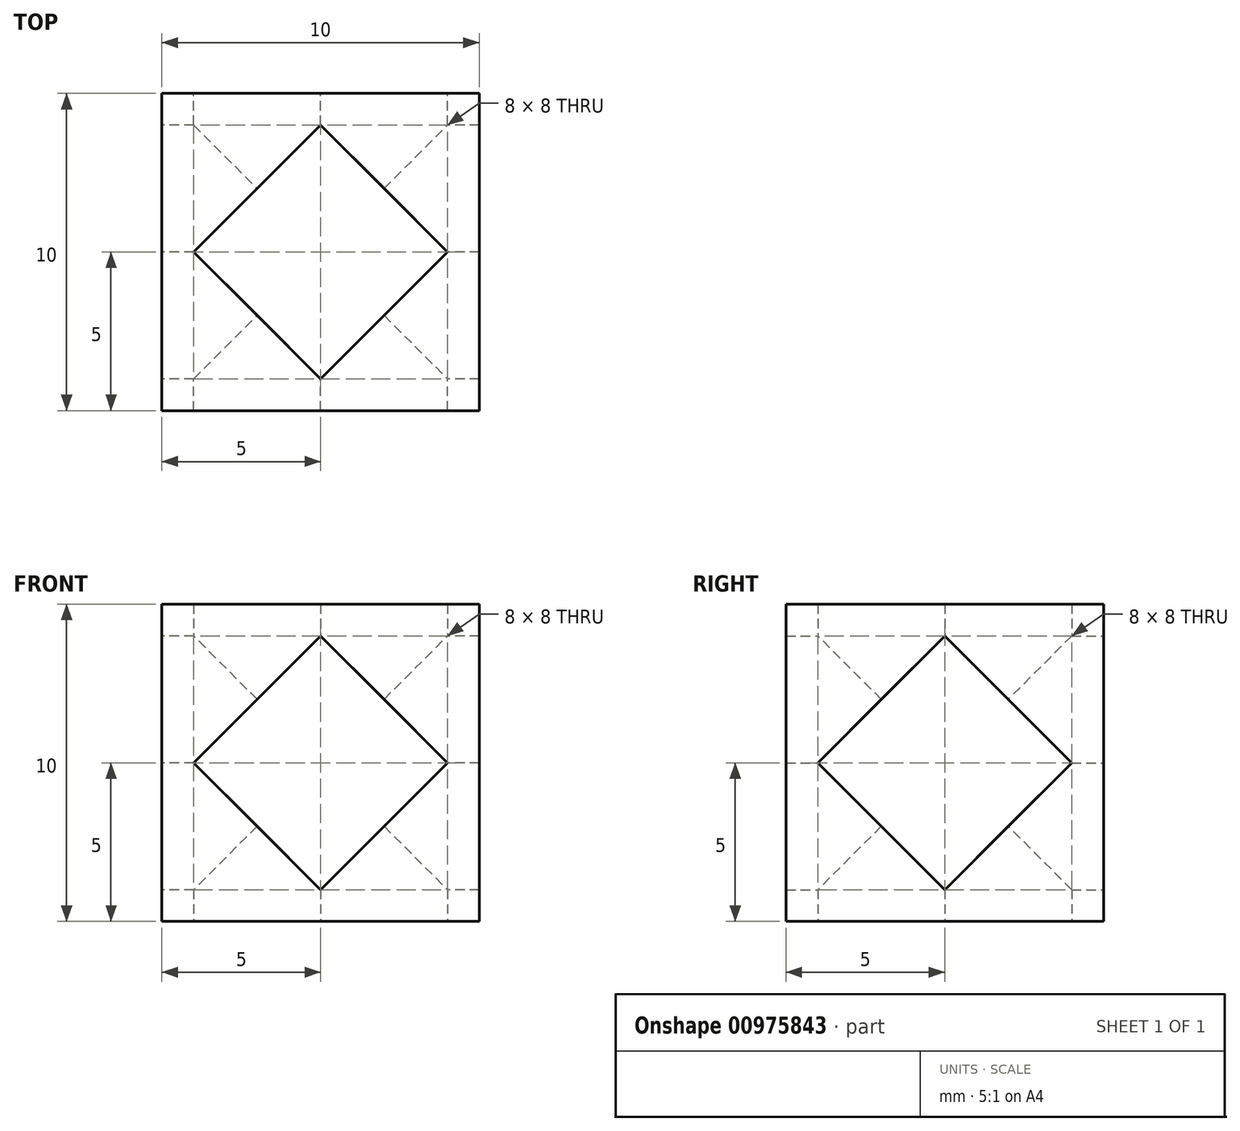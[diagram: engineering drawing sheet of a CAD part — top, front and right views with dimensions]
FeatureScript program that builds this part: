
annotation { "Feature Type Name" : "Feature", "Feature Type Description" : "" }
export const myFeature = defineFeature(function(context is Context, id is Id, definition is map)
    precondition{}
    {
        {
            var Q0;
            Q0=qCreatedBy(makeId("Front.planeOp"),FACE);
            var sketch = newSketch(context, id + "F0", { "sketchPlane" : qUnion([Q0])});
            skLineSegment(sketch, "E0.bottom", {"start": v(5, 5) * mm, "end": v(-5, 5) * mm});
            skLineSegment(sketch, "E0.top", {"start": v(5, -5) * mm, "end": v(-5, -5) * mm});
            skLineSegment(sketch, "E0.left", {"start": v(5, 5) * mm, "end": v(5, -5) * mm});
            skLineSegment(sketch, "E0.right", {"start": v(-5, 5) * mm, "end": v(-5, -5) * mm});
            skPoint(sketch, "E0.middle", {"position": v(0, 0) * mm});
            skLineSegment(sketch, "E1", {"start": v(0, 4) * mm, "end": v(-4, 0) * mm});
            skLineSegment(sketch, "E2", {"start": v(-4, 0) * mm, "end": v(0, -4) * mm});
            skLineSegment(sketch, "E3", {"start": v(0, -4) * mm, "end": v(4, 0) * mm});
            skLineSegment(sketch, "E4", {"start": v(4, 0) * mm, "end": v(0, 4) * mm});
            skSolve(sketch);
        }
        {
            var Q0;
            Q0=qCreatedBy(makeId("Right.planeOp"),FACE);
            var sketch = newSketch(context, id + "F1", { "sketchPlane" : qUnion([Q0])});
            skLineSegment(sketch, "E5.bottom", {"start": v(5, 5) * mm, "end": v(-5, 5) * mm});
            skLineSegment(sketch, "E5.top", {"start": v(5, -5) * mm, "end": v(-5, -5) * mm});
            skLineSegment(sketch, "E5.left", {"start": v(5, 5) * mm, "end": v(5, -5) * mm});
            skLineSegment(sketch, "E5.right", {"start": v(-5, 5) * mm, "end": v(-5, -5) * mm});
            skPoint(sketch, "E5.middle", {"position": v(0, 0) * mm});
            skLineSegment(sketch, "E6", {"start": v(0, 4) * mm, "end": v(-4, 0) * mm});
            skLineSegment(sketch, "E7", {"start": v(-4, 0) * mm, "end": v(0, -4) * mm});
            skLineSegment(sketch, "E8", {"start": v(0, -4) * mm, "end": v(4, 0) * mm});
            skLineSegment(sketch, "E9", {"start": v(4, 0) * mm, "end": v(0, 4) * mm});
            skSolve(sketch);
        }
        {
            var Q0;
            Q0=qCreatedBy(makeId("Top.planeOp"),FACE);
            var sketch = newSketch(context, id + "F2", { "sketchPlane" : qUnion([Q0])});
            skLineSegment(sketch, "E10.bottom", {"start": v(5, 5) * mm, "end": v(-5, 5) * mm});
            skLineSegment(sketch, "E10.top", {"start": v(5, -5) * mm, "end": v(-5, -5) * mm});
            skLineSegment(sketch, "E10.left", {"start": v(5, 5) * mm, "end": v(5, -5) * mm});
            skLineSegment(sketch, "E10.right", {"start": v(-5, 5) * mm, "end": v(-5, -5) * mm});
            skPoint(sketch, "E10.middle", {"position": v(0, 0) * mm});
            skLineSegment(sketch, "E11", {"start": v(0, 4) * mm, "end": v(-4, 0) * mm});
            skLineSegment(sketch, "E12", {"start": v(-4, 0) * mm, "end": v(0, -4) * mm});
            skLineSegment(sketch, "E13", {"start": v(0, -4) * mm, "end": v(4, 0) * mm});
            skLineSegment(sketch, "E14", {"start": v(4, 0) * mm, "end": v(0, 4) * mm});
            skSolve(sketch);
        }
        {
            var Q0;
            Q0 = qSketchRegion(id + "F0", true);
            extrude(context, id + "F3", {"entities" : qUnion([Q0]), "endBound" : BoundingType.SYMMETRIC, "depth" : 10 * mm, "offsetDistance" : 25 * mm});
        }
        {
            var Q0;
            Q0 = qSketchRegion(id + "F1", true);
            extrude(context, id + "F4", {"entities" : qUnion([Q0]), "operationType" : NewBodyOperationType.INTERSECT, "endBound" : BoundingType.SYMMETRIC, "depth" : 10 * mm, "offsetDistance" : 25 * mm});
        }
        {
            var Q0;
            Q0 = qSketchRegion(id + "F2", true);
            extrude(context, id + "F5", {"entities" : qUnion([Q0]), "operationType" : NewBodyOperationType.INTERSECT, "endBound" : BoundingType.SYMMETRIC, "depth" : 10 * mm, "offsetDistance" : 25 * mm});
        }
    });
